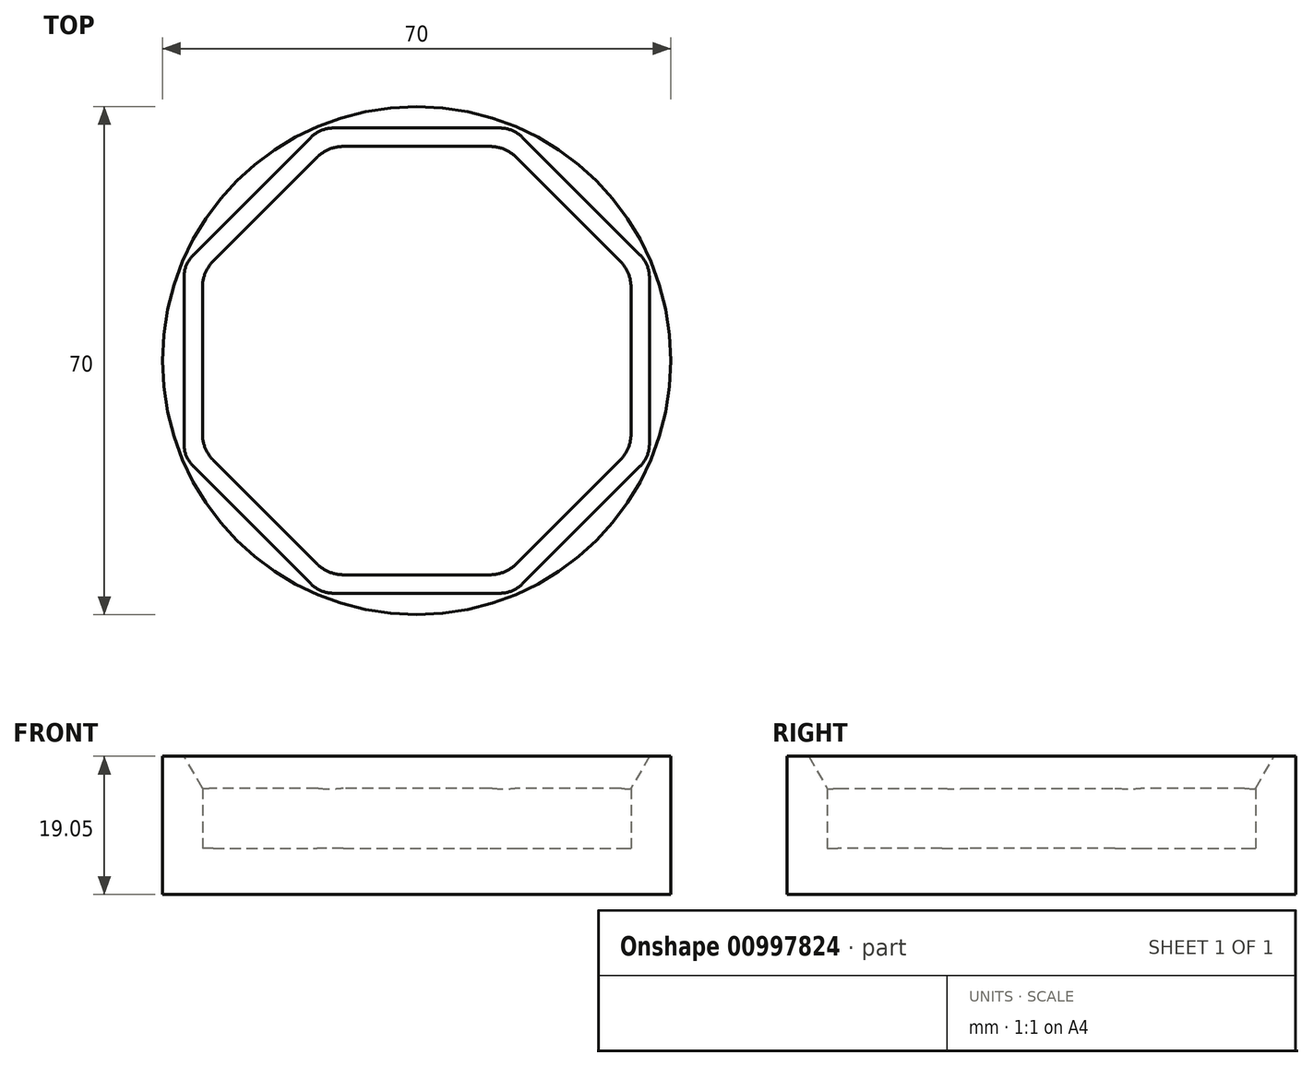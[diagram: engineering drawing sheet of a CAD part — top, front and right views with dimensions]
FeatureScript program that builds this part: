
annotation { "Feature Type Name" : "Feature", "Feature Type Description" : "" }
export const myFeature = defineFeature(function(context is Context, id is Id, definition is map)
    precondition{}
    {
        {
            var Q0;
            Q0=qCreatedBy(makeId("Top.planeOp"),FACE);
            var sketch = newSketch(context, id + "F0", { "sketchPlane" : qUnion([Q0])});
            skCircle(sketch, "E0", {"center": v(0, 0) * mm, "radius": 35 * mm});
            skSolve(sketch);
        }
        {
            var Q0;
            Q0 = qSketchRegion(id + "F0", true);
            extrude(context, id + "F1", {"entities" : qUnion([Q0]), "depth" : 6.35 * mm, "offsetDistance" : 25.4 * mm});
        }
        {
            var Q0;
            Q0=makeQuery(id+"F1.opExtrude","CAP_FACE",FACE,{"disambiguationData":[OSD([sQuery(id+"F0.wireOp",EDGE,"E0")])],"isStart":false});
            var sketch = newSketch(context, id + "F2", { "sketchPlane" : qUnion([Q0])});
            skCircle(sketch, "E1.cCircle", {"center": v(0, 0) * mm, "radius": 29.5 * mm, "construction": true});
            skLineSegment(sketch, "E1.0", {"start": v(-12.22, 29.5) * mm, "end": v(12.22, 29.5) * mm});
            skLineSegment(sketch, "E1.1", {"start": v(12.22, 29.5) * mm, "end": v(29.5, 12.22) * mm});
            skLineSegment(sketch, "E1.2", {"start": v(29.5, 12.22) * mm, "end": v(29.5, -12.22) * mm});
            skLineSegment(sketch, "E1.3", {"start": v(29.5, -12.22) * mm, "end": v(12.22, -29.5) * mm});
            skLineSegment(sketch, "E1.4", {"start": v(12.22, -29.5) * mm, "end": v(-12.22, -29.5) * mm});
            skLineSegment(sketch, "E1.5", {"start": v(-12.22, -29.5) * mm, "end": v(-29.5, -12.22) * mm});
            skLineSegment(sketch, "E1.6", {"start": v(-29.5, -12.22) * mm, "end": v(-29.5, 12.22) * mm});
            skLineSegment(sketch, "E1.7", {"start": v(-29.5, 12.22) * mm, "end": v(-12.22, 29.5) * mm});
            skPoint(sketch, "E1.0.midPoint", {"position": v(0, 29.5) * mm});
            skCircle(sketch, "E2", {"center": v(0, 0) * mm, "radius": 35 * mm});
            skSolve(sketch);
        }
        {
            var Q0;
            Q0=makeQuery(id+"F2.imprint","IMPRINT",FACE,{"disambiguationData":[TD([[makeQuery(id+"F2.imprint","IMPRINT",EDGE,{"derivedFrom":sQuery(id+"F2.wireOp",EDGE,"E1.0")}),1.0]])]});
            extrude(context, id + "F3", {"entities" : qUnion([Q0]), "operationType" : NewBodyOperationType.ADD, "depth" : 12.7 * mm, "offsetDistance" : 25.4 * mm});
        }
        {
            var Q0;
            Q0=makeQuery(id+"F3.opExtrude","CAP_EDGE",EDGE,{"disambiguationData":[OSD([sQuery(id+"F2.wireOp",EDGE,"E1.6")])],"isStart":false});
            var Q1;
            Q1=makeQuery(id+"F3.opExtrude","CAP_EDGE",EDGE,{"disambiguationData":[OSD([sQuery(id+"F2.wireOp",EDGE,"E1.7")])],"isStart":false});
            var Q2;
            Q2=makeQuery(id+"F3.opExtrude","CAP_EDGE",EDGE,{"disambiguationData":[OSD([sQuery(id+"F2.wireOp",EDGE,"E1.0")])],"isStart":false});
            var Q3;
            Q3=makeQuery(id+"F3.opExtrude","CAP_EDGE",EDGE,{"disambiguationData":[OSD([sQuery(id+"F2.wireOp",EDGE,"E1.1")])],"isStart":false});
            var Q4;
            Q4=makeQuery(id+"F3.opExtrude","CAP_EDGE",EDGE,{"disambiguationData":[OSD([sQuery(id+"F2.wireOp",EDGE,"E1.2")])],"isStart":false});
            var Q5;
            Q5=makeQuery(id+"F3.opExtrude","CAP_EDGE",EDGE,{"disambiguationData":[OSD([sQuery(id+"F2.wireOp",EDGE,"E1.3")])],"isStart":false});
            var Q6;
            Q6=makeQuery(id+"F3.opExtrude","CAP_EDGE",EDGE,{"disambiguationData":[OSD([sQuery(id+"F2.wireOp",EDGE,"E1.4")])],"isStart":false});
            var Q7;
            Q7=makeQuery(id+"F3.opExtrude","CAP_EDGE",EDGE,{"disambiguationData":[OSD([sQuery(id+"F2.wireOp",EDGE,"E1.5")])],"isStart":false});
            chamfer(context, id + "F4", {"entities" : qUnion([Q0, Q1, Q2, Q3, Q4, Q5, Q6, Q7]), "chamferType" : ChamferType.OFFSET_ANGLE, "width" : 2.54 * mm, "oppositeDirection" : false, "angle" : 60 * degree, "tangentPropagation" : true});
        }
        {
            var Q0;
            Q0=makeQuery(id+"F4.opChamfer","BLEND_EDGE",EDGE,{"blendedFrom":[makeQuery(id+"F3.opExtrude","CAP_EDGE",EDGE,{"disambiguationData":[OSD([sQuery(id+"F2.wireOp",EDGE,"E1.0")])],"isStart":false}),makeQuery(id+"F3.opExtrude","CAP_EDGE",EDGE,{"disambiguationData":[OSD([sQuery(id+"F2.wireOp",EDGE,"E1.7")])],"isStart":false})],"blendedInto":[]});
            var Q1;
            Q1=makeQuery(id+"F4.opChamfer","BLEND_EDGE",EDGE,{"blendedFrom":[makeQuery(id+"F3.opExtrude","CAP_EDGE",EDGE,{"disambiguationData":[OSD([sQuery(id+"F2.wireOp",EDGE,"E1.0")])],"isStart":false}),makeQuery(id+"F3.opExtrude","CAP_EDGE",EDGE,{"disambiguationData":[OSD([sQuery(id+"F2.wireOp",EDGE,"E1.1")])],"isStart":false})],"blendedInto":[]});
            var Q2;
            Q2=makeQuery(id+"F3.opExtrude","SWEPT_EDGE",EDGE,{"disambiguationData":[OSD([sQuery(id+"F2.wireOp",EDGE,"E1.0"),sQuery(id+"F2.wireOp",EDGE,"E1.1")])]});
            var Q3;
            Q3=makeQuery(id+"F3.opExtrude","SWEPT_EDGE",EDGE,{"disambiguationData":[OSD([sQuery(id+"F2.wireOp",EDGE,"E1.0"),sQuery(id+"F2.wireOp",EDGE,"E1.7")])]});
            var Q4;
            Q4=makeQuery(id+"F3.opExtrude","SWEPT_EDGE",EDGE,{"disambiguationData":[OSD([sQuery(id+"F2.wireOp",EDGE,"E1.6"),sQuery(id+"F2.wireOp",EDGE,"E1.7")])]});
            var Q5;
            Q5=makeQuery(id+"F4.opChamfer","BLEND_EDGE",EDGE,{"blendedFrom":[makeQuery(id+"F3.opExtrude","CAP_EDGE",EDGE,{"disambiguationData":[OSD([sQuery(id+"F2.wireOp",EDGE,"E1.6")])],"isStart":false}),makeQuery(id+"F3.opExtrude","CAP_EDGE",EDGE,{"disambiguationData":[OSD([sQuery(id+"F2.wireOp",EDGE,"E1.7")])],"isStart":false})],"blendedInto":[]});
            var Q6;
            Q6=makeQuery(id+"F4.opChamfer","BLEND_EDGE",EDGE,{"blendedFrom":[makeQuery(id+"F3.opExtrude","CAP_EDGE",EDGE,{"disambiguationData":[OSD([sQuery(id+"F2.wireOp",EDGE,"E1.5")])],"isStart":false}),makeQuery(id+"F3.opExtrude","CAP_EDGE",EDGE,{"disambiguationData":[OSD([sQuery(id+"F2.wireOp",EDGE,"E1.6")])],"isStart":false})],"blendedInto":[]});
            var Q7;
            Q7=makeQuery(id+"F3.opExtrude","SWEPT_EDGE",EDGE,{"disambiguationData":[OSD([sQuery(id+"F2.wireOp",EDGE,"E1.5"),sQuery(id+"F2.wireOp",EDGE,"E1.6")])]});
            var Q8;
            Q8=makeQuery(id+"F3.opExtrude","SWEPT_EDGE",EDGE,{"disambiguationData":[OSD([sQuery(id+"F2.wireOp",EDGE,"E1.4"),sQuery(id+"F2.wireOp",EDGE,"E1.5")])]});
            var Q9;
            Q9=makeQuery(id+"F4.opChamfer","BLEND_EDGE",EDGE,{"blendedFrom":[makeQuery(id+"F3.opExtrude","CAP_EDGE",EDGE,{"disambiguationData":[OSD([sQuery(id+"F2.wireOp",EDGE,"E1.4")])],"isStart":false}),makeQuery(id+"F3.opExtrude","CAP_EDGE",EDGE,{"disambiguationData":[OSD([sQuery(id+"F2.wireOp",EDGE,"E1.5")])],"isStart":false})],"blendedInto":[]});
            var Q10;
            Q10=makeQuery(id+"F3.opExtrude","SWEPT_EDGE",EDGE,{"disambiguationData":[OSD([sQuery(id+"F2.wireOp",EDGE,"E1.1"),sQuery(id+"F2.wireOp",EDGE,"E1.2")])]});
            var Q11;
            Q11=makeQuery(id+"F4.opChamfer","BLEND_EDGE",EDGE,{"blendedFrom":[makeQuery(id+"F3.opExtrude","CAP_EDGE",EDGE,{"disambiguationData":[OSD([sQuery(id+"F2.wireOp",EDGE,"E1.1")])],"isStart":false}),makeQuery(id+"F3.opExtrude","CAP_EDGE",EDGE,{"disambiguationData":[OSD([sQuery(id+"F2.wireOp",EDGE,"E1.2")])],"isStart":false})],"blendedInto":[]});
            var Q12;
            Q12=makeQuery(id+"F4.opChamfer","BLEND_EDGE",EDGE,{"blendedFrom":[makeQuery(id+"F3.opExtrude","CAP_EDGE",EDGE,{"disambiguationData":[OSD([sQuery(id+"F2.wireOp",EDGE,"E1.2")])],"isStart":false}),makeQuery(id+"F3.opExtrude","CAP_EDGE",EDGE,{"disambiguationData":[OSD([sQuery(id+"F2.wireOp",EDGE,"E1.3")])],"isStart":false})],"blendedInto":[]});
            var Q13;
            Q13=makeQuery(id+"F3.opExtrude","SWEPT_EDGE",EDGE,{"disambiguationData":[OSD([sQuery(id+"F2.wireOp",EDGE,"E1.2"),sQuery(id+"F2.wireOp",EDGE,"E1.3")])]});
            var Q14;
            Q14=makeQuery(id+"F3.opExtrude","SWEPT_EDGE",EDGE,{"disambiguationData":[OSD([sQuery(id+"F2.wireOp",EDGE,"E1.3"),sQuery(id+"F2.wireOp",EDGE,"E1.4")])]});
            var Q15;
            Q15=makeQuery(id+"F4.opChamfer","BLEND_EDGE",EDGE,{"blendedFrom":[makeQuery(id+"F3.opExtrude","CAP_EDGE",EDGE,{"disambiguationData":[OSD([sQuery(id+"F2.wireOp",EDGE,"E1.3")])],"isStart":false}),makeQuery(id+"F3.opExtrude","CAP_EDGE",EDGE,{"disambiguationData":[OSD([sQuery(id+"F2.wireOp",EDGE,"E1.4")])],"isStart":false})],"blendedInto":[]});
            fillet(context, id + "F5", {"entities" : qUnion([Q0, Q1, Q2, Q3, Q4, Q5, Q6, Q7, Q8, Q9, Q10, Q11, Q12, Q13, Q14, Q15]), "radius" : 5.08 * mm, "tangentPropagation" : true, "allowEdgeOverflow" : false});
        }
    });
